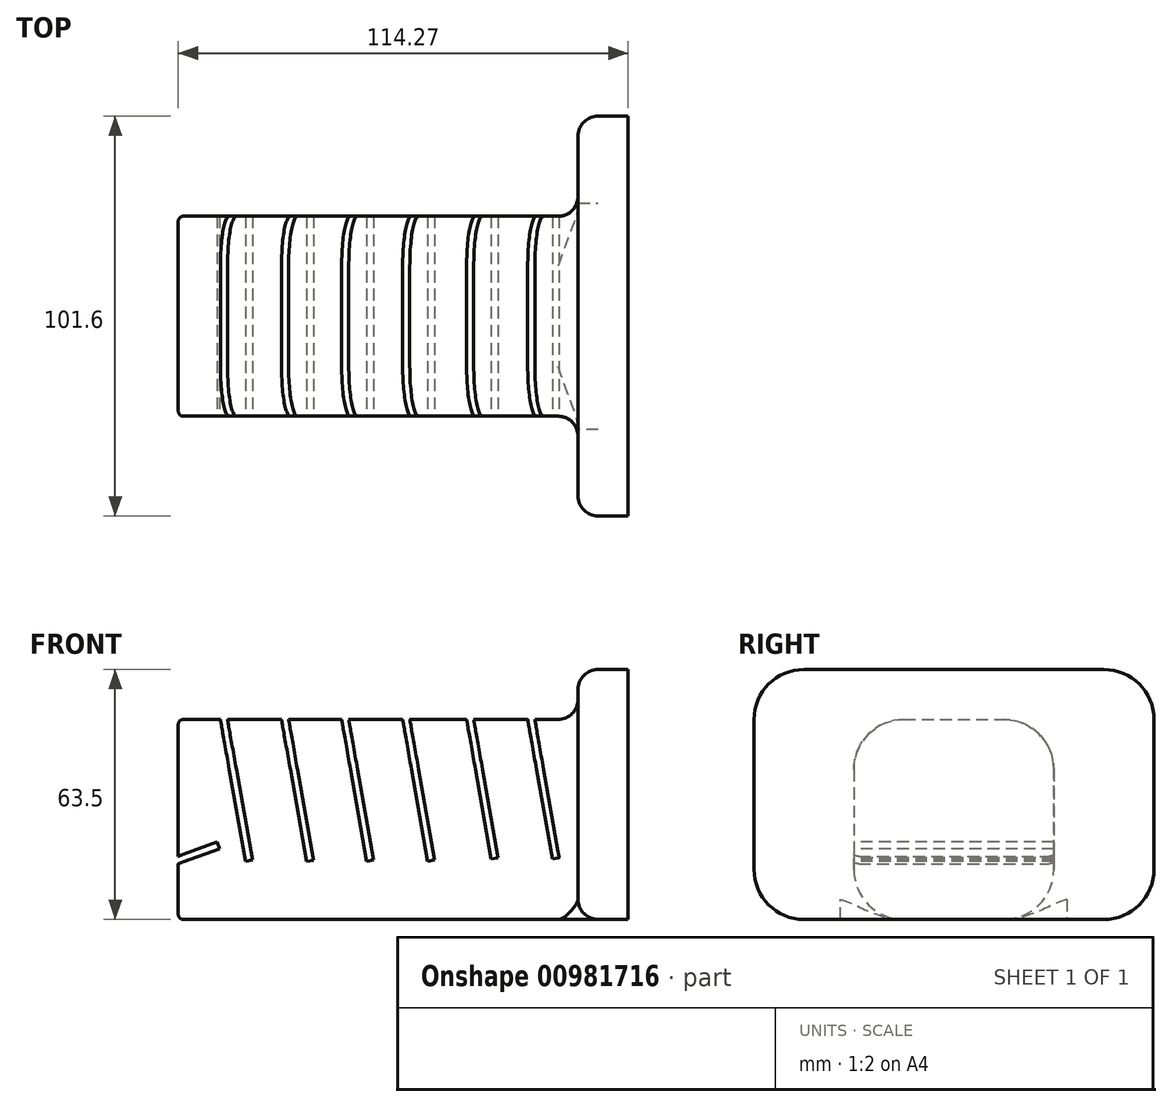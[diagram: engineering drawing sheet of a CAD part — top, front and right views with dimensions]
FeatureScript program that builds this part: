
annotation { "Feature Type Name" : "Feature", "Feature Type Description" : "" }
export const myFeature = defineFeature(function(context is Context, id is Id, definition is map)
    precondition{}
    {
        {
            var Q0;
            Q0=qCreatedBy(makeId("Top.planeOp"),FACE);
            var sketch = newSketch(context, id + "F0", { "sketchPlane" : qUnion([Q0])});
            skLineSegment(sketch, "E0.bottom", {"start": v(50.8, -25.4) * mm, "end": v(-50.8, -25.4) * mm});
            skLineSegment(sketch, "E0.top", {"start": v(50.8, 25.4) * mm, "end": v(-50.8, 25.4) * mm});
            skLineSegment(sketch, "E0.left", {"start": v(50.8, -25.4) * mm, "end": v(50.8, 25.4) * mm});
            skLineSegment(sketch, "E0.right", {"start": v(-50.8, -25.4) * mm, "end": v(-50.8, 25.4) * mm});
            skPoint(sketch, "E0.middle", {"position": v(0, 0) * mm});
            skSolve(sketch);
        }
        {
            var Q0;
            Q0=qCreatedBy(makeId("Top.planeOp"),FACE);
            var sketch = newSketch(context, id + "F1", { "sketchPlane" : qUnion([Q0])});
            skLineSegment(sketch, "E1.bottom", {"start": v(50.77, 50.85) * mm, "end": v(63.47, 50.85) * mm});
            skLineSegment(sketch, "E1.top", {"start": v(50.77, -50.75) * mm, "end": v(63.47, -50.75) * mm});
            skLineSegment(sketch, "E1.left", {"start": v(50.77, 50.85) * mm, "end": v(50.77, -50.75) * mm});
            skLineSegment(sketch, "E1.right", {"start": v(63.47, 50.85) * mm, "end": v(63.47, -50.75) * mm});
            skSolve(sketch);
        }
        {
            var Q0;
            Q0 = qSketchRegion(id + "F0", true);
            extrude(context, id + "F2", {"entities" : qUnion([Q0]), "depth" : 50.8 * mm, "offsetDistance" : 25.4 * mm});
        }
        {
            var Q0;
            Q0=makeQuery(id+"F2.opExtrude","SWEPT_FACE",FACE,{"disambiguationData":[OSD([sQuery(id+"F0.wireOp",EDGE,"E0.bottom")])]});
            var sketch = newSketch(context, id + "F3", { "sketchPlane" : qUnion([Q0])});
            skLineSegment(sketch, "E2.bottom", {"start": v(-40.13, 51.02) * mm, "end": v(-38.38, 51.33) * mm});
            skLineSegment(sketch, "E2.top", {"start": v(-33.74, 14.75) * mm, "end": v(-31.99, 15.06) * mm});
            skLineSegment(sketch, "E2.left", {"start": v(-40.13, 51.02) * mm, "end": v(-33.74, 14.75) * mm});
            skLineSegment(sketch, "E2.right", {"start": v(-38.38, 51.33) * mm, "end": v(-31.99, 15.06) * mm});
            skLineSegment(sketch, "E3.bottom", {"start": v(-24.61, 51.02) * mm, "end": v(-22.86, 51.32) * mm});
            skLineSegment(sketch, "E3.top", {"start": v(-18.22, 14.75) * mm, "end": v(-16.47, 15.05) * mm});
            skLineSegment(sketch, "E3.left", {"start": v(-24.61, 51.02) * mm, "end": v(-18.22, 14.75) * mm});
            skLineSegment(sketch, "E3.right", {"start": v(-22.86, 51.32) * mm, "end": v(-16.47, 15.05) * mm});
            skLineSegment(sketch, "E4.bottom", {"start": v(-9.35, 51.05) * mm, "end": v(-7.6, 51.35) * mm});
            skLineSegment(sketch, "E4.top", {"start": v(-2.95, 14.77) * mm, "end": v(-1.2, 15.08) * mm});
            skLineSegment(sketch, "E4.left", {"start": v(-9.35, 51.05) * mm, "end": v(-2.95, 14.77) * mm});
            skLineSegment(sketch, "E4.right", {"start": v(-7.6, 51.35) * mm, "end": v(-1.2, 15.08) * mm});
            skLineSegment(sketch, "E5.bottom", {"start": v(6.17, 51.04) * mm, "end": v(7.92, 51.35) * mm});
            skLineSegment(sketch, "E5.top", {"start": v(12.57, 14.77) * mm, "end": v(14.32, 15.08) * mm});
            skLineSegment(sketch, "E5.left", {"start": v(6.17, 51.04) * mm, "end": v(12.57, 14.77) * mm});
            skLineSegment(sketch, "E5.right", {"start": v(7.92, 51.35) * mm, "end": v(14.32, 15.08) * mm});
            skLineSegment(sketch, "E6.bottom", {"start": v(22.3, 51.63) * mm, "end": v(24.05, 51.94) * mm});
            skLineSegment(sketch, "E6.top", {"start": v(28.7, 15.36) * mm, "end": v(30.44, 15.67) * mm});
            skLineSegment(sketch, "E6.left", {"start": v(22.3, 51.63) * mm, "end": v(28.7, 15.36) * mm});
            skLineSegment(sketch, "E6.right", {"start": v(24.05, 51.94) * mm, "end": v(30.44, 15.67) * mm});
            skLineSegment(sketch, "E7.bottom", {"start": v(37.82, 51.63) * mm, "end": v(39.57, 51.94) * mm});
            skLineSegment(sketch, "E7.top", {"start": v(44.21, 15.36) * mm, "end": v(45.96, 15.67) * mm});
            skLineSegment(sketch, "E7.left", {"start": v(37.82, 51.63) * mm, "end": v(44.21, 15.36) * mm});
            skLineSegment(sketch, "E7.right", {"start": v(39.57, 51.94) * mm, "end": v(45.96, 15.67) * mm});
            skSolve(sketch);
        }
        {
            var Q0;
            Q0 = qSketchRegion(id + "F3", true);
            extrude(context, id + "F4", {"entities" : qUnion([Q0]), "operationType" : NewBodyOperationType.REMOVE, "oppositeDirection" : true, "depth" : 57.15 * mm, "offsetDistance" : 25.4 * mm});
        }
        {
            var Q0;
            Q0 = qSketchRegion(id + "F1", true);
            extrude(context, id + "F5", {"entities" : qUnion([Q0]), "operationType" : NewBodyOperationType.ADD, "depth" : 63.5 * mm, "offsetDistance" : 25.4 * mm});
        }
        {
            var Q0;
            Q0=makeQuery(id+"F2.opExtrude","SWEPT_FACE",FACE,{"disambiguationData":[OSD([sQuery(id+"F0.wireOp",EDGE,"E0.bottom")])]});
            var sketch = newSketch(context, id + "F6", { "sketchPlane" : qUnion([Q0])});
            skLineSegment(sketch, "E8.bottom", {"start": v(-40.88, 19.65) * mm, "end": v(-51.62, 15.74) * mm});
            skLineSegment(sketch, "E8.top", {"start": v(-40.27, 17.98) * mm, "end": v(-51.01, 14.07) * mm});
            skLineSegment(sketch, "E8.left", {"start": v(-40.88, 19.65) * mm, "end": v(-40.27, 17.98) * mm});
            skLineSegment(sketch, "E8.right", {"start": v(-51.62, 15.74) * mm, "end": v(-51.01, 14.07) * mm});
            skSolve(sketch);
        }
        {
            var Q0;
            Q0 = qSketchRegion(id + "F6", true);
            extrude(context, id + "F7", {"entities" : qUnion([Q0]), "operationType" : NewBodyOperationType.REMOVE, "oppositeDirection" : true, "depth" : 55.27 * mm, "offsetDistance" : 25.4 * mm});
        }
        {
            var Q0;
            Q0=makeQuery(id+"F2.opExtrude","CAP_EDGE",EDGE,{"disambiguationData":[OSD([sQuery(id+"F0.wireOp",EDGE,"E0.bottom")])],"isStart":true});
            var Q1;
            {var subQ0=sQuery(id+"F0.wireOp",EDGE,"E0.bottom");var subQ1=sQuery(id+"F0.wireOp",EDGE,"E0.right");Q1=makeQuery(id+"F4.boolean.opBoolean","SPLIT",EDGE,{"disambiguationData":[TD([makeQuery(id+"F2.opExtrude","SWEPT_FACE",FACE,{"disambiguationData":[OSD([subQ1])]})])],"derivedFrom":makeQuery(id+"F2.opExtrude","CAP_EDGE",EDGE,{"disambiguationData":[OSD([subQ0])],"isStart":false})});}
            var Q2;
            {var subQ0=sQuery(id+"F0.wireOp",EDGE,"E0.bottom");Q2=makeQuery(id+"F4.boolean.opBoolean","SPLIT",EDGE,{"disambiguationData":[TD([makeQuery(id+"F4.opExtrude","SWEPT_FACE",FACE,{"disambiguationData":[OSD([sQuery(id+"F3.wireOp",EDGE,"E2.right")])]})])],"derivedFrom":makeQuery(id+"F2.opExtrude","CAP_EDGE",EDGE,{"disambiguationData":[OSD([subQ0])],"isStart":false})});}
            var Q3;
            {var subQ0=sQuery(id+"F0.wireOp",EDGE,"E0.bottom");Q3=makeQuery(id+"F4.boolean.opBoolean","SPLIT",EDGE,{"disambiguationData":[TD([makeQuery(id+"F4.opExtrude","SWEPT_FACE",FACE,{"disambiguationData":[OSD([sQuery(id+"F3.wireOp",EDGE,"E3.right")])]})])],"derivedFrom":makeQuery(id+"F2.opExtrude","CAP_EDGE",EDGE,{"disambiguationData":[OSD([subQ0])],"isStart":false})});}
            var Q4;
            {var subQ0=sQuery(id+"F0.wireOp",EDGE,"E0.bottom");Q4=makeQuery(id+"F4.boolean.opBoolean","SPLIT",EDGE,{"disambiguationData":[TD([makeQuery(id+"F4.opExtrude","SWEPT_FACE",FACE,{"disambiguationData":[OSD([sQuery(id+"F3.wireOp",EDGE,"E4.right")])]})])],"derivedFrom":makeQuery(id+"F2.opExtrude","CAP_EDGE",EDGE,{"disambiguationData":[OSD([subQ0])],"isStart":false})});}
            var Q5;
            {var subQ0=sQuery(id+"F0.wireOp",EDGE,"E0.bottom");Q5=makeQuery(id+"F4.boolean.opBoolean","SPLIT",EDGE,{"disambiguationData":[TD([makeQuery(id+"F4.opExtrude","SWEPT_FACE",FACE,{"disambiguationData":[OSD([sQuery(id+"F3.wireOp",EDGE,"E5.right")])]})])],"derivedFrom":makeQuery(id+"F2.opExtrude","CAP_EDGE",EDGE,{"disambiguationData":[OSD([subQ0])],"isStart":false})});}
            var Q6;
            {var subQ0=sQuery(id+"F0.wireOp",EDGE,"E0.bottom");Q6=makeQuery(id+"F4.boolean.opBoolean","SPLIT",EDGE,{"disambiguationData":[TD([makeQuery(id+"F4.opExtrude","SWEPT_FACE",FACE,{"disambiguationData":[OSD([sQuery(id+"F3.wireOp",EDGE,"E6.right")])]})])],"derivedFrom":makeQuery(id+"F2.opExtrude","CAP_EDGE",EDGE,{"disambiguationData":[OSD([subQ0])],"isStart":false})});}
            var Q7;
            {var subQ0=sQuery(id+"F0.wireOp",EDGE,"E0.bottom");var subQ1=sQuery(id+"F0.wireOp",EDGE,"E0.left");Q7=makeQuery(id+"F4.boolean.opBoolean","SPLIT",EDGE,{"disambiguationData":[TD([makeQuery(id+"F2.opExtrude","SWEPT_FACE",FACE,{"disambiguationData":[OSD([subQ1])]})])],"derivedFrom":makeQuery(id+"F2.opExtrude","CAP_EDGE",EDGE,{"disambiguationData":[OSD([subQ0])],"isStart":false})});}
            var Q8;
            {var subQ0=sQuery(id+"F0.wireOp",EDGE,"E0.left");var subQ1=sQuery(id+"F0.wireOp",EDGE,"E0.top");Q8=makeQuery(id+"F4.boolean.opBoolean","SPLIT",EDGE,{"disambiguationData":[TD([makeQuery(id+"F2.opExtrude","SWEPT_FACE",FACE,{"disambiguationData":[OSD([subQ0])]})])],"derivedFrom":makeQuery(id+"F2.opExtrude","CAP_EDGE",EDGE,{"disambiguationData":[OSD([subQ1])],"isStart":false})});}
            var Q9;
            {var subQ0=sQuery(id+"F0.wireOp",EDGE,"E0.top");Q9=makeQuery(id+"F4.boolean.opBoolean","SPLIT",EDGE,{"disambiguationData":[TD([makeQuery(id+"F4.opExtrude","SWEPT_FACE",FACE,{"disambiguationData":[OSD([sQuery(id+"F3.wireOp",EDGE,"E6.right")])]})])],"derivedFrom":makeQuery(id+"F2.opExtrude","CAP_EDGE",EDGE,{"disambiguationData":[OSD([subQ0])],"isStart":false})});}
            var Q10;
            {var subQ0=sQuery(id+"F0.wireOp",EDGE,"E0.top");Q10=makeQuery(id+"F4.boolean.opBoolean","SPLIT",EDGE,{"disambiguationData":[TD([makeQuery(id+"F4.opExtrude","SWEPT_FACE",FACE,{"disambiguationData":[OSD([sQuery(id+"F3.wireOp",EDGE,"E5.right")])]})])],"derivedFrom":makeQuery(id+"F2.opExtrude","CAP_EDGE",EDGE,{"disambiguationData":[OSD([subQ0])],"isStart":false})});}
            var Q11;
            {var subQ0=sQuery(id+"F0.wireOp",EDGE,"E0.top");Q11=makeQuery(id+"F4.boolean.opBoolean","SPLIT",EDGE,{"disambiguationData":[TD([makeQuery(id+"F4.opExtrude","SWEPT_FACE",FACE,{"disambiguationData":[OSD([sQuery(id+"F3.wireOp",EDGE,"E4.right")])]})])],"derivedFrom":makeQuery(id+"F2.opExtrude","CAP_EDGE",EDGE,{"disambiguationData":[OSD([subQ0])],"isStart":false})});}
            var Q12;
            {var subQ0=sQuery(id+"F0.wireOp",EDGE,"E0.top");Q12=makeQuery(id+"F4.boolean.opBoolean","SPLIT",EDGE,{"disambiguationData":[TD([makeQuery(id+"F4.opExtrude","SWEPT_FACE",FACE,{"disambiguationData":[OSD([sQuery(id+"F3.wireOp",EDGE,"E3.right")])]})])],"derivedFrom":makeQuery(id+"F2.opExtrude","CAP_EDGE",EDGE,{"disambiguationData":[OSD([subQ0])],"isStart":false})});}
            var Q13;
            {var subQ0=sQuery(id+"F0.wireOp",EDGE,"E0.top");Q13=makeQuery(id+"F4.boolean.opBoolean","SPLIT",EDGE,{"disambiguationData":[TD([makeQuery(id+"F4.opExtrude","SWEPT_FACE",FACE,{"disambiguationData":[OSD([sQuery(id+"F3.wireOp",EDGE,"E2.right")])]})])],"derivedFrom":makeQuery(id+"F2.opExtrude","CAP_EDGE",EDGE,{"disambiguationData":[OSD([subQ0])],"isStart":false})});}
            var Q14;
            {var subQ0=sQuery(id+"F0.wireOp",EDGE,"E0.right");var subQ1=sQuery(id+"F0.wireOp",EDGE,"E0.top");Q14=makeQuery(id+"F4.boolean.opBoolean","SPLIT",EDGE,{"disambiguationData":[TD([makeQuery(id+"F2.opExtrude","SWEPT_FACE",FACE,{"disambiguationData":[OSD([subQ0])]})])],"derivedFrom":makeQuery(id+"F2.opExtrude","CAP_EDGE",EDGE,{"disambiguationData":[OSD([subQ1])],"isStart":false})});}
            var Q15;
            Q15=makeQuery(id+"F2.opExtrude","CAP_EDGE",EDGE,{"disambiguationData":[OSD([sQuery(id+"F0.wireOp",EDGE,"E0.top")])],"isStart":true});
            fillet(context, id + "F8", {"entities" : qUnion([Q0, Q1, Q2, Q3, Q4, Q5, Q6, Q7, Q8, Q9, Q10, Q11, Q12, Q13, Q14, Q15]), "radius" : 12.7 * mm, "tangentPropagation" : true, "allowEdgeOverflow" : false});
        }
        {
            var Q0;
            Q0=makeQuery(id+"F5.opExtrude","CAP_EDGE",EDGE,{"disambiguationData":[OSD([sQuery(id+"F1.wireOp",EDGE,"E1.top")])],"isStart":false});
            var Q1;
            Q1=makeQuery(id+"F5.opExtrude","CAP_EDGE",EDGE,{"disambiguationData":[OSD([sQuery(id+"F1.wireOp",EDGE,"E1.top")])],"isStart":true});
            var Q2;
            Q2=makeQuery(id+"F5.opExtrude","CAP_EDGE",EDGE,{"disambiguationData":[OSD([sQuery(id+"F1.wireOp",EDGE,"E1.bottom")])],"isStart":false});
            var Q3;
            Q3=makeQuery(id+"F5.opExtrude","CAP_EDGE",EDGE,{"disambiguationData":[OSD([sQuery(id+"F1.wireOp",EDGE,"E1.bottom")])],"isStart":true});
            fillet(context, id + "F9", {"entities" : qUnion([Q0, Q1, Q2, Q3]), "radius" : 12.7 * mm, "tangentPropagation" : true, "allowEdgeOverflow" : false});
        }
        {
            var Q0;
            Q0=makeQuery(id+"F5.opExtrude","SWEPT_FACE",FACE,{"disambiguationData":[OSD([sQuery(id+"F1.wireOp",EDGE,"E1.left")])]});
            fillet(context, id + "F10", {"entities" : qUnion([Q0]), "radius" : 5.08 * mm, "tangentPropagation" : true, "allowEdgeOverflow" : false});
        }
        {
            var Q0;
            Q0=makeQuery(id+"F2.opExtrude","CAP_EDGE",EDGE,{"disambiguationData":[OSD([sQuery(id+"F0.wireOp",EDGE,"E0.right")])],"isStart":false});
            var Q1;
            Q1=makeQuery(id+"F2.opExtrude","CAP_EDGE",EDGE,{"disambiguationData":[OSD([sQuery(id+"F0.wireOp",EDGE,"E0.right")])],"isStart":true});
            fillet(context, id + "F11", {"entities" : qUnion([Q0, Q1]), "radius" : 1.27 * mm, "tangentPropagation" : true, "allowEdgeOverflow" : false});
        }
    });
